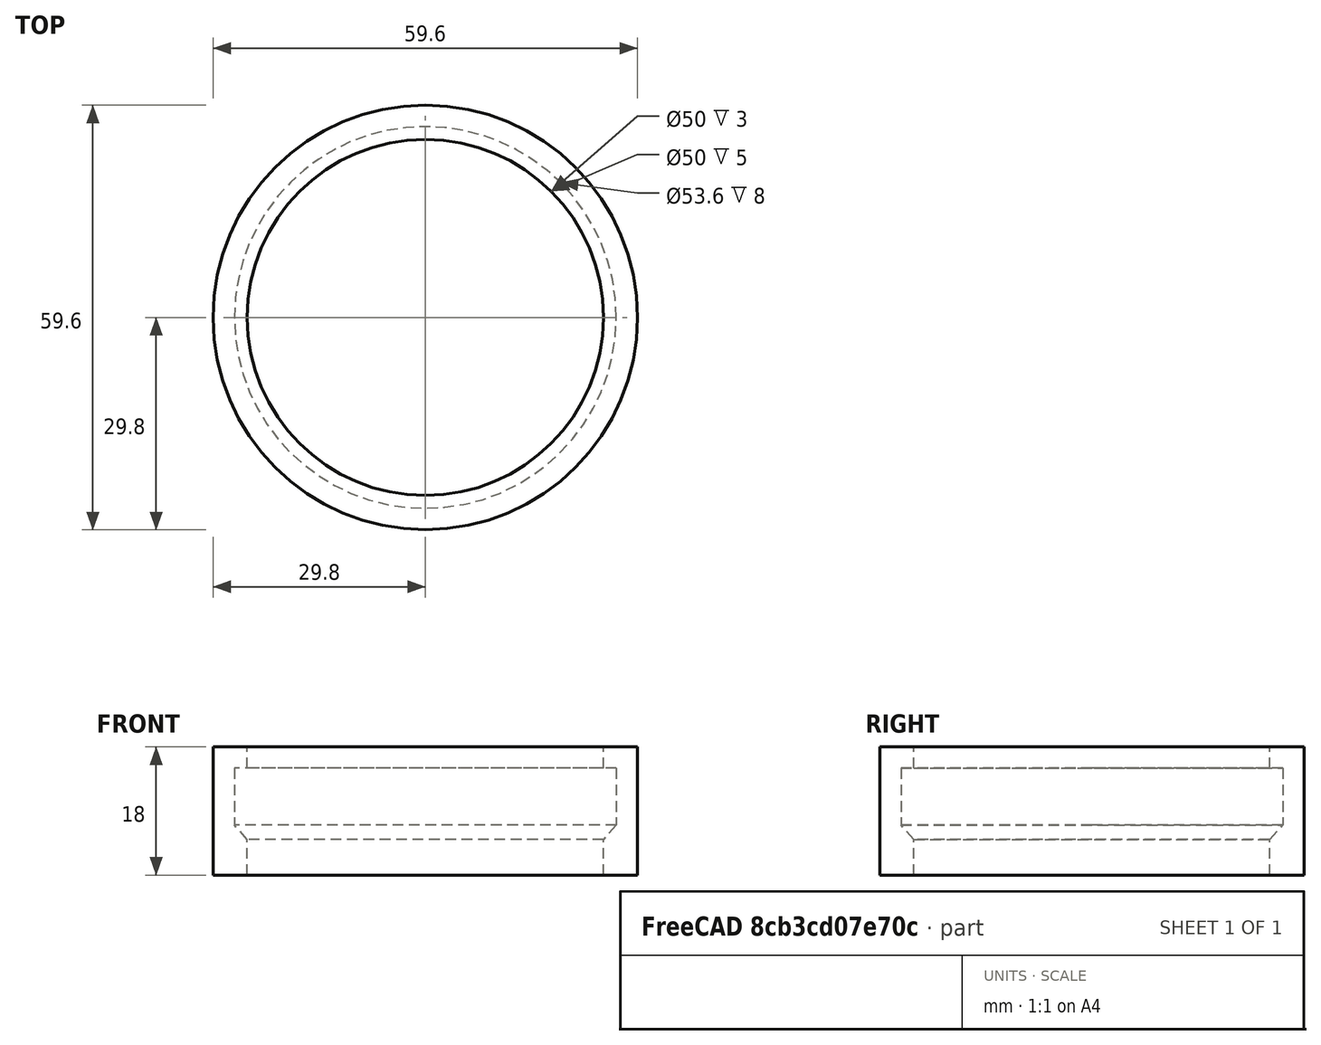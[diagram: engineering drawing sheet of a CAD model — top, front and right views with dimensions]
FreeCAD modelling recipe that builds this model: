
FCSTD DOCUMENT  (FreeCAD 1.1R39748 (Git))
Label: горло
License: All rights reserved
LicenseURL: https://en.wikipedia.org/wiki/All_rights_reserved
objects: App::Point×1, Sketcher::SketchObject×1, PartDesign::Revolution×1, PartDesign::Body×1
note: 6 computed .brp shape members not serialized (recipe doc carries the construction recipe); baked Part::Feature solids carry a one-line shape summary decoded from their .brp

FEATURE [App::Point] Origin001
  Role = Origin
FEATURE [Sketcher::SketchObject] Sketch
  ArcFitTolerance = 1e-06
  AttachmentSupport = -> [XZ_Plane]
  ExternalTypes = [0]
  FullyConstrained = true
  MakeInternals = false
  MapMode = 5
  Placement = pos=(0,0,0) rot=(1,0,0;1.5708rad)
  expr: Constraints[23] = 63 / 2 - 1.8 + 0.3
  expr: Constraints[2] = 50 / 2 + 0.5
  sketch-geometry (8):
    g0: LineSegment StartX=25.5 StartY=0 StartZ=0 EndX=25.5 EndY=5 EndZ=0
    g1: LineSegment StartX=30 StartY=17.5 StartZ=0 EndX=30 EndY=9.5 EndZ=0
    g2: LineSegment StartX=30 StartY=9.5 StartZ=0 EndX=25.5 EndY=5 EndZ=0
    g3: LineSegment StartX=30 StartY=17.5 StartZ=0 EndX=25 EndY=17.5 EndZ=0
    g4: LineSegment StartX=25 StartY=17.5 StartZ=0 EndX=25 EndY=20.5 EndZ=0
    g5: LineSegment StartX=25 StartY=20.5 StartZ=0 EndX=32 EndY=20.5 EndZ=0
    g6: LineSegment StartX=32 StartY=20.5 StartZ=0 EndX=32 EndY=0 EndZ=0
    g7: LineSegment StartX=32 StartY=0 StartZ=0 EndX=25.5 EndY=0 EndZ=0
  constraints (25):
    c: PointOnObject(g0,g-1)
    c: Vertical(g0)
    c: Distance(g0,g-1) = 25.5
    c: Vertical(g1)
    c: Coincident(g2,g0)
    c: Coincident(g1,g2)
    c: Distance(g1,g1) = 8
    c: Coincident(g3,g1)
    c: Horizontal(g3)
    c: DistanceX(g-1,g3) = 25
    c: Coincident(g4,g3)
    c: Vertical(g4)
    c: Coincident(g5,g4)
    c: Horizontal(g5)
    c: Coincident(g6,g5)
    c: PointOnObject(g6,g-1)
    c: Vertical(g6)
    c: Coincident(g7,g6)
    c: Coincident(g7,g0)
    c: Distance(g3,g4) = 3
    c: DistanceX(g1,g6) = 2
    c: DistanceY(g0,g0) = 5
    c: Angle(g0,g2) = 2.35619
    c: DistanceX(g-1,g1) = 30
    c: Distance(g3,g1) = 5
FEATURE [PartDesign::Revolution] Revolution
  Angle = 360
  Angle2 = 60
  Axis = (0,2e-16,1)
  Base = (0,0,0)
  Placement = pos=(0,0,0) rot=(1,0,0;1.5708rad)
  Profile = -> Sketch
  ReferenceAxis = -> Sketch [V_Axis]
  Reversed = true
  Suppressed = false
  Type = 0
FEATURE [PartDesign::Body] Body
  AllowCompound = false
  Group = -> [Sketch,Revolution]
  Origin = -> Origin
  Tip = -> Revolution
